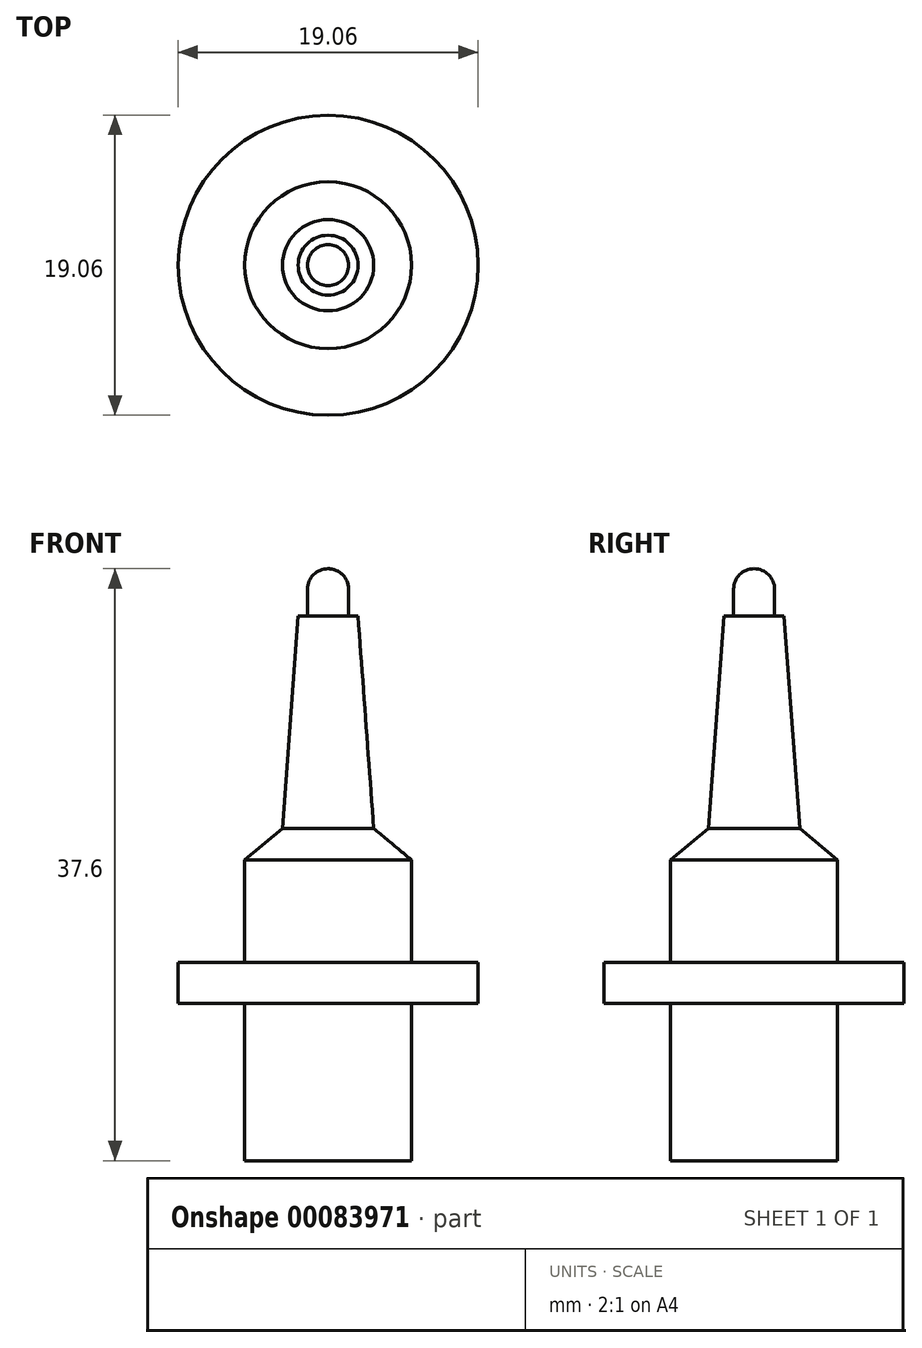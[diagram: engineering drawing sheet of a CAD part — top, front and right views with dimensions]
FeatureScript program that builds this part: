
annotation { "Feature Type Name" : "Feature", "Feature Type Description" : "" }
export const myFeature = defineFeature(function(context is Context, id is Id, definition is map)
    precondition{}
    {
        {
            var Q0;
            Q0=qCreatedBy(makeId("Front.planeOp"),FACE);
            var sketch = newSketch(context, id + "F0", { "sketchPlane" : qUnion([Q0])});
            skLineSegment(sketch, "E0", {"start": v(0, 0) * mm, "end": v(-9.53, 0) * mm});
            skLineSegment(sketch, "E1", {"start": v(-9.53, 0) * mm, "end": v(-9.53, -2.6) * mm});
            skLineSegment(sketch, "E2", {"start": v(-9.53, -2.6) * mm, "end": v(0, -2.6) * mm});
            skLineSegment(sketch, "E3", {"start": v(0, -2.6) * mm, "end": v(0, 0) * mm});
            skLineSegment(sketch, "E4", {"start": v(-5.3, 0) * mm, "end": v(-5.3, 6.5) * mm});
            skLineSegment(sketch, "E5", {"start": v(-5.3, 6.5) * mm, "end": v(-2.9, 8.5) * mm});
            skLineSegment(sketch, "E6", {"start": v(-2.9, 8.5) * mm, "end": v(-1.9, 22) * mm});
            skLineSegment(sketch, "E7", {"start": v(-1.9, 22) * mm, "end": v(0, 22) * mm});
            skLineSegment(sketch, "E8", {"start": v(0, 22) * mm, "end": v(0, 0) * mm});
            skLineSegment(sketch, "E9", {"start": v(0, 22) * mm, "end": v(0, 25) * mm});
            skLineSegment(sketch, "E10", {"start": v(-1.3, 22) * mm, "end": v(-1.3, 23.7) * mm});
            skArc(sketch, "E11", {"start": v(0, 25) * mm, "mid": v(-0.92, 24.62) * mm, "end": v(-1.3, 23.7) * mm});
            skLineSegment(sketch, "E12", {"start": v(0, -2.6) * mm, "end": v(0, -12.6) * mm});
            skLineSegment(sketch, "E13", {"start": v(0, -12.6) * mm, "end": v(-5.3, -12.6) * mm});
            skLineSegment(sketch, "E14", {"start": v(-5.3, -12.6) * mm, "end": v(-5.3, -2.6) * mm});
            skSolve(sketch);
        }
        {
            var Q0;
            Q0 = qSketchRegion(id + "F0", true);
            var Q1;
            Q1=sQuery(id+"F0.wireOp",EDGE,"E8");
            revolve(context, id + "F1", {"entities" : qUnion([Q0]), "axis" : qUnion([Q1]), "revolveType" : RevolveType.FULL});
        }
    });
